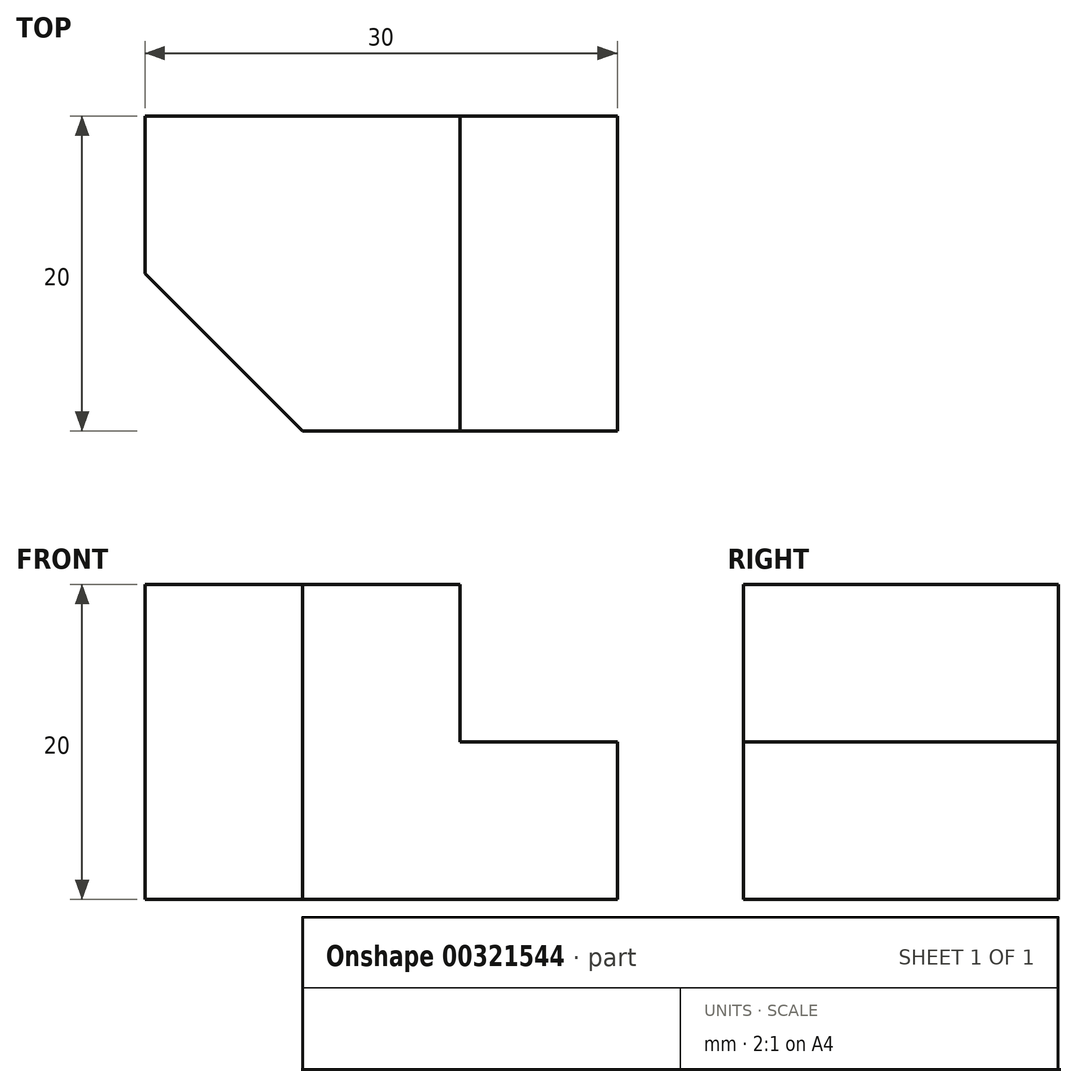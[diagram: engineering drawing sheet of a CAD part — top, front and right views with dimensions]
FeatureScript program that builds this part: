
annotation { "Feature Type Name" : "Feature", "Feature Type Description" : "" }
export const myFeature = defineFeature(function(context is Context, id is Id, definition is map)
    precondition{}
    {
        {
            var Q0;
            Q0=qCreatedBy(makeId("Front.planeOp"),FACE);
            var sketch = newSketch(context, id + "F0", { "sketchPlane" : qUnion([Q0])});
            skLineSegment(sketch, "E0", {"start": v(0, 0) * mm, "end": v(0, 20) * mm});
            skLineSegment(sketch, "E1", {"start": v(0, 20) * mm, "end": v(10, 20) * mm});
            skLineSegment(sketch, "E2", {"start": v(10, 20) * mm, "end": v(10, 0) * mm});
            skLineSegment(sketch, "E3", {"start": v(10, 0) * mm, "end": v(0, 0) * mm});
            skLineSegment(sketch, "E4", {"start": v(10, 20) * mm, "end": v(20, 20) * mm});
            skLineSegment(sketch, "E5", {"start": v(20, 20) * mm, "end": v(20, 10) * mm});
            skLineSegment(sketch, "E6", {"start": v(20, 10) * mm, "end": v(30, 10) * mm});
            skLineSegment(sketch, "E7", {"start": v(30, 10) * mm, "end": v(30, 0) * mm});
            skLineSegment(sketch, "E8", {"start": v(30, 0) * mm, "end": v(10, 0) * mm});
            skSolve(sketch);
        }
        {
            var Q0;
            Q0 = qSketchRegion(id + "F0", true);
            extrude(context, id + "F1", {"entities" : qUnion([Q0]), "depth" : 20 * mm});
        }
        {
            var Q0;
            Q0=makeQuery(id+"F1.opExtrude","SWEPT_FACE",FACE,{"disambiguationData":[OSD([sQuery(id+"F0.wireOp",EDGE,"E1"),sQuery(id+"F0.wireOp",EDGE,"E4")])]});
            var sketch = newSketch(context, id + "F2", { "sketchPlane" : qUnion([Q0])});
            skLineSegment(sketch, "E9", {"start": v(0, -20) * mm, "end": v(0, -10) * mm});
            skLineSegment(sketch, "E10", {"start": v(0, -10) * mm, "end": v(10, -20) * mm});
            skLineSegment(sketch, "E11", {"start": v(10, -20) * mm, "end": v(0, -20) * mm});
            skSolve(sketch);
        }
        {
            var Q0;
            Q0 = qSketchRegion(id + "F2", true);
            extrude(context, id + "F3", {"entities" : qUnion([Q0]), "operationType" : NewBodyOperationType.REMOVE, "oppositeDirection" : true, "depth" : 25 * mm});
        }
    });
